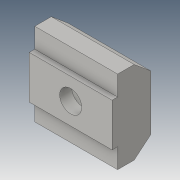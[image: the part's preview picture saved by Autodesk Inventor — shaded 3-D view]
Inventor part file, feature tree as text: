
AUTODESK INVENTOR PART (.ipt)
format: ipt  version: 2016 (Build 200138000, 138)  size: 130,560 bytes
history: native  units: in
note: dims shown in document units (in); Inventor stores cm internally (conversion verified against a paired STEP export)
features: extrude x2, sketch x2, hole x1, chamfer x1
ambient origin geometry x8: Origin, YZ Plane, XZ Plane, XY Plane, X Axis, Y Axis, Z Axis, Center Point
bodies: Solid1 (feature_tree)
feature tree (6):
  extrude  "Extrusion1"  Depth=0.5906in
  extrude  "Extrusion2"  Depth=0.3937in
  hole  "Hole2"  [1 undecoded]
  chamfer  "Chamfer1"  Distance=0.3071in
  sketch  "Sketch1"  dims[d0=0.5906in d1=0.1181in]
  sketch  "Sketch2"  dims[d2=0.1181in d5=0.3937in d6=0.8919in d7=0.3071in d8=0.0394in d9=0.2362in d10=0.5906in d11=0.0in d12=0.3228in d14=0.189in d15=0.0in d25=0.2953in d26=0.2953in d27=0.2953in d28=0.2953in d29=0.1575in d30=0.75in d31=0.375in d32=0.25in d33=0.5635in d34=1.0in d35=0.8108in d36=0.02in d37=0.125in d38=45.0deg]
note: 1 required parameter value undecoded (feature->parameter linkage not recoverable at this tier; creation-order binding heuristic only, values carry confidence <= 0.55)
